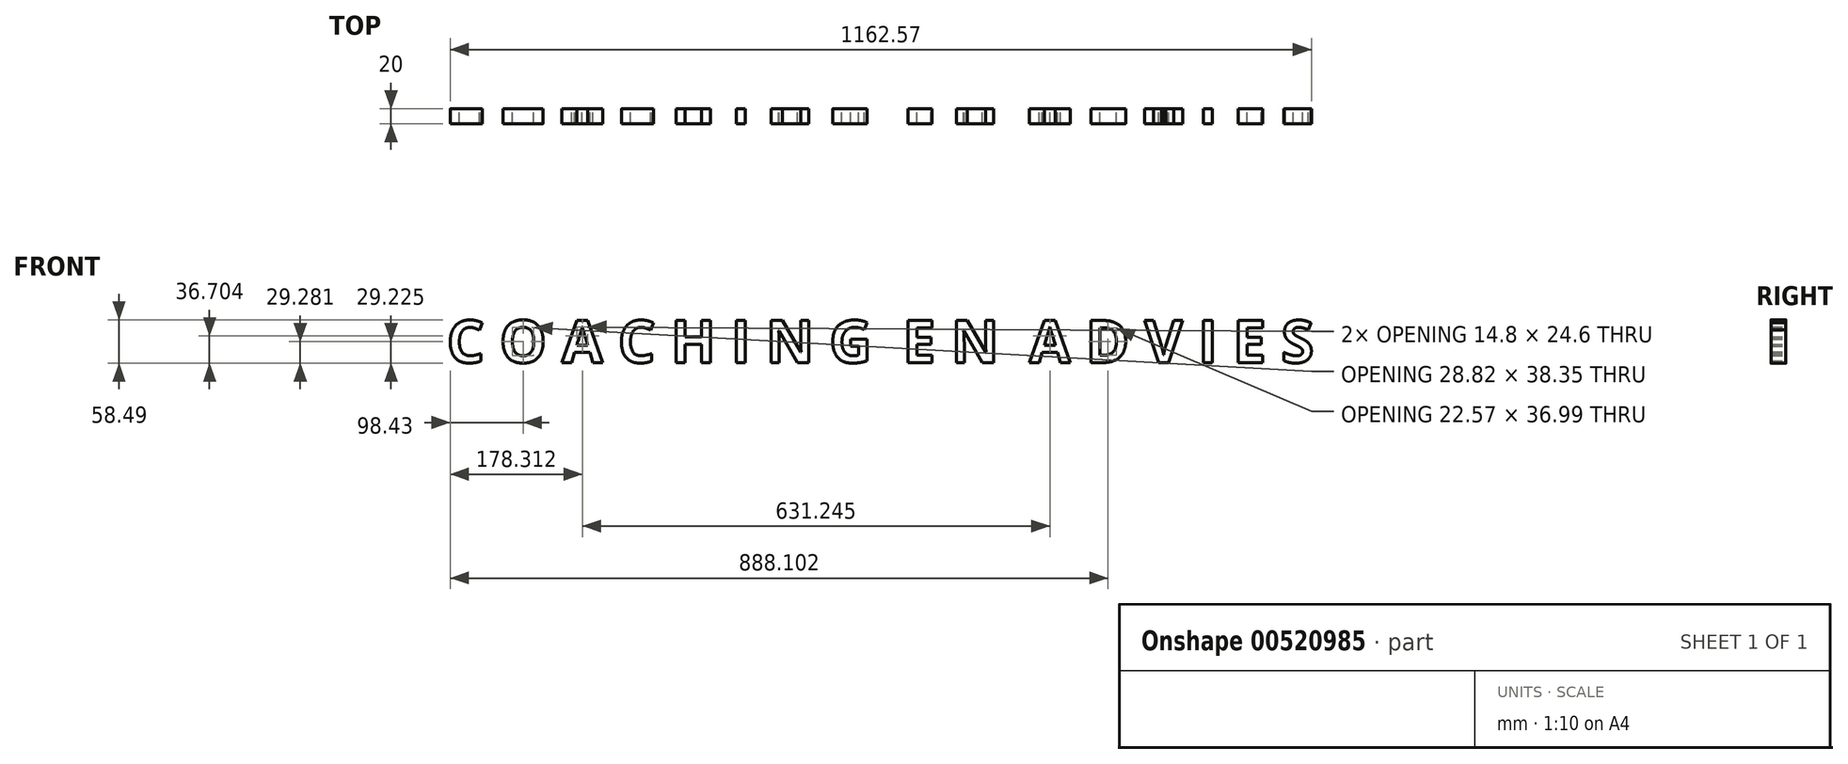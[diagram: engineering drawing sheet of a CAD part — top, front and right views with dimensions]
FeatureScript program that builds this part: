
annotation { "Feature Type Name" : "Feature", "Feature Type Description" : "" }
export const myFeature = defineFeature(function(context is Context, id is Id, definition is map)
    precondition{}
    {
        {
            var Q0;
            Q0=qCreatedBy(makeId("Front.planeOp"),FACE);
            var sketch = newSketch(context, id + "F0", { "sketchPlane" : qUnion([Q0])});
            skText(sketch, "E0", { "text": "C O A C H I N G  E N  A D V I E S", "fontName": "OpenSans-Bold.ttf"});
            const initialGuessF0  = {"E0": [-0.06027, -0.01304, 1, 0, 0.0573]};
            skSetInitialGuess(sketch, initialGuessF0);
            skSolve(sketch);
        }
        {
            var Q0;
            Q0 = qSketchRegion(id + "F0", true);
            extrude(context, id + "F1", {"entities" : qUnion([Q0]), "depth" : 20 * mm, "offsetDistance" : 25 * mm});
        }
    });
